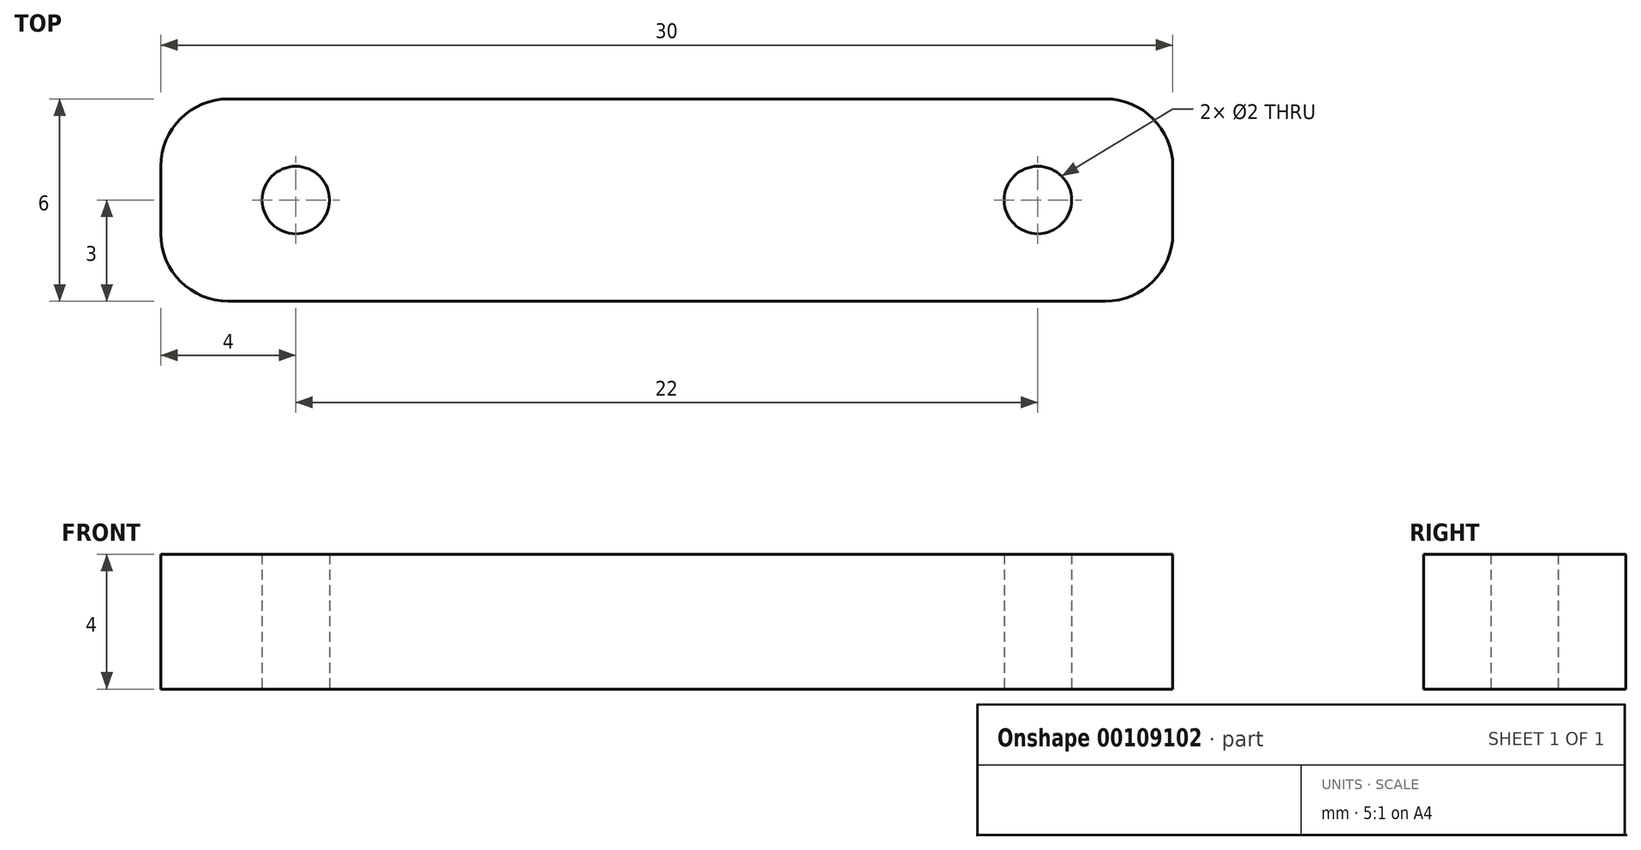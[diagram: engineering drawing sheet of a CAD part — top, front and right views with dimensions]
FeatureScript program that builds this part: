
annotation { "Feature Type Name" : "Feature", "Feature Type Description" : "" }
export const myFeature = defineFeature(function(context is Context, id is Id, definition is map)
    precondition{}
    {
        {
            var Q0;
            Q0=qCreatedBy(makeId("Top.planeOp"),FACE);
            var sketch = newSketch(context, id + "F0", { "sketchPlane" : qUnion([Q0])});
            skLineSegment(sketch, "E0.bottom", {"start": v(-13, 3) * mm, "end": v(13, 3) * mm});
            skLineSegment(sketch, "E0.top", {"start": v(-13, -3) * mm, "end": v(13, -3) * mm});
            skLineSegment(sketch, "E0.left", {"start": v(-15, 1) * mm, "end": v(-15, -1) * mm});
            skLineSegment(sketch, "E0.right", {"start": v(15, 1) * mm, "end": v(15, -1) * mm});
            skPoint(sketch, "E0.middle", {"position": v(0, 0) * mm});
            skCircle(sketch, "E1", {"center": v(-11, 0) * mm, "radius": 1 * mm});
            skCircle(sketch, "E2", {"center": v(11, 0) * mm, "radius": 1 * mm});
            skPoint(sketch, "E3.visualSharp", {"position": v(-15, 3) * mm});
            skArc(sketch, "E3.filletArc", {"start": v(-13, 3) * mm, "mid": v(-14.41, 2.41) * mm, "end": v(-15, 1) * mm});
            skPoint(sketch, "E4.visualSharp", {"position": v(-15, -3) * mm});
            skArc(sketch, "E4.filletArc", {"start": v(-15, -1) * mm, "mid": v(-14.41, -2.41) * mm, "end": v(-13, -3) * mm});
            skPoint(sketch, "E5.visualSharp", {"position": v(15, 3) * mm});
            skArc(sketch, "E5.filletArc", {"start": v(15, 1) * mm, "mid": v(14.41, 2.41) * mm, "end": v(13, 3) * mm});
            skPoint(sketch, "E6.visualSharp", {"position": v(15, -3) * mm});
            skArc(sketch, "E6.filletArc", {"start": v(13, -3) * mm, "mid": v(14.41, -2.41) * mm, "end": v(15, -1) * mm});
            skSolve(sketch);
        }
        {
            var Q0;
            Q0=makeQuery(id+"F0.imprint","IMPRINT",FACE,{"disambiguationData":[TD([[makeQuery(id+"F0.imprint","IMPRINT",EDGE,{"derivedFrom":sQuery(id+"F0.wireOp",EDGE,"E0.bottom")}),-1.0]])]});
            extrude(context, id + "F1", {"entities" : qUnion([Q0]), "depth" : 4 * mm});
        }
    });
